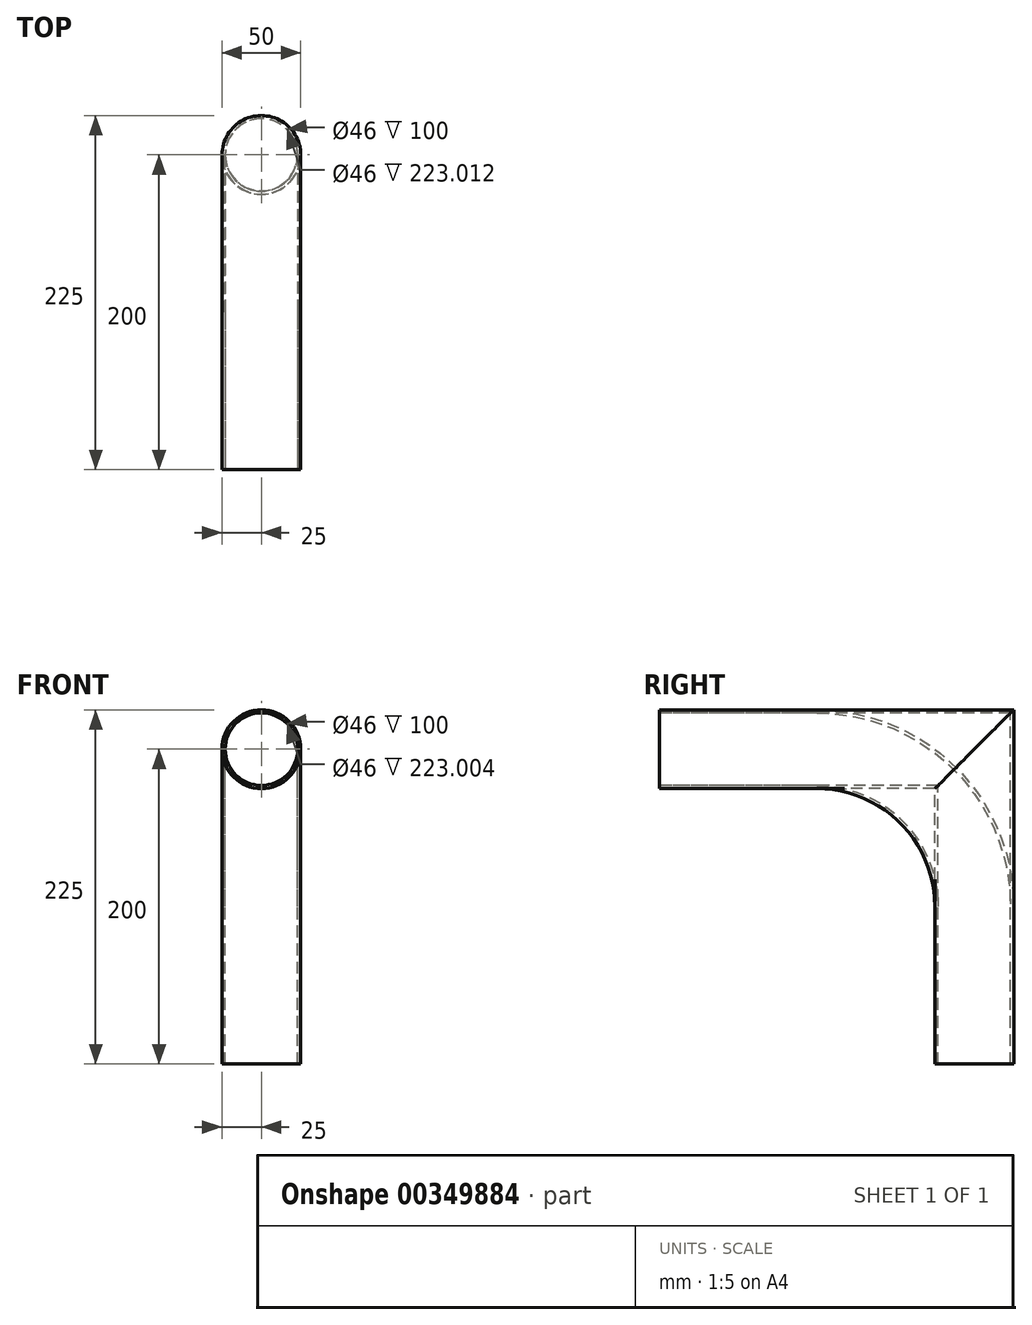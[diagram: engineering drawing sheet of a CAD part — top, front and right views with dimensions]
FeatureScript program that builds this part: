
annotation { "Feature Type Name" : "Feature", "Feature Type Description" : "" }
export const myFeature = defineFeature(function(context is Context, id is Id, definition is map)
    precondition{}
    {
        {
            var Q0;
            Q0=qCreatedBy(makeId("Top.planeOp"),FACE);
            var sketch = newSketch(context, id + "F0", { "sketchPlane" : qUnion([Q0])});
            skCircle(sketch, "E0", {"center": v(0, 0) * mm, "radius": 25 * mm});
            skCircle(sketch, "E1", {"center": v(0, 0) * mm, "radius": 23 * mm});
            skSolve(sketch);
        }
        {
            var Q0;
            Q0=qCreatedBy(makeId("Right.planeOp"),FACE);
            var sketch = newSketch(context, id + "F1", { "sketchPlane" : qUnion([Q0])});
            skArc(sketch, "E2", {"start": v(0, 100) * mm, "mid": v(-29.29, 170.71) * mm, "end": v(-100, 200) * mm});
            skLineSegment(sketch, "E3", {"start": v(-100, 200) * mm, "end": v(-200, 200) * mm});
            skLineSegment(sketch, "E4", {"start": v(0, 100) * mm, "end": v(0, 0) * mm});
            skSolve(sketch);
        }
        {
            var Q0;
            Q0=makeQuery(id+"F0.imprint","IMPRINT",FACE,{"disambiguationData":[TD([[makeQuery(id+"F0.imprint","IMPRINT",EDGE,{"derivedFrom":sQuery(id+"F0.wireOp",EDGE,"E0")}),1.0]])]});
            var Q1;
            Q1 = qConstructionFilter(qBodyType(qCreatedBy(id + "F1" ,EDGE), BodyType.WIRE), ConstructionObject.NO);
            sweep(context, id + "F2", {"profiles" : qUnion([Q0]), "path" : qUnion([Q1])});
        }
        {
            var Q0;
            Q0=qCreatedBy(makeId("Right.planeOp"),FACE);
            var sketch = newSketch(context, id + "F3", { "sketchPlane" : qUnion([Q0])});
            skLineSegment(sketch, "E5", {"start": v(0, 0) * mm, "end": v(0, 200) * mm});
            skLineSegment(sketch, "E6", {"start": v(0, 200) * mm, "end": v(-200, 200) * mm});
            skSolve(sketch);
        }
        {
            var Q0;
            Q0=makeQuery(id+"F0.imprint","IMPRINT",FACE,{"disambiguationData":[TD([[makeQuery(id+"F0.imprint","IMPRINT",EDGE,{"derivedFrom":sQuery(id+"F0.wireOp",EDGE,"E0")}),1.0]])]});
            var Q1;
            Q1 = qConstructionFilter(qBodyType(qCreatedBy(id + "F3" ,EDGE), BodyType.WIRE), ConstructionObject.NO);
            sweep(context, id + "F4", {"profiles" : qUnion([Q0]), "path" : qUnion([Q1])});
        }
    });
